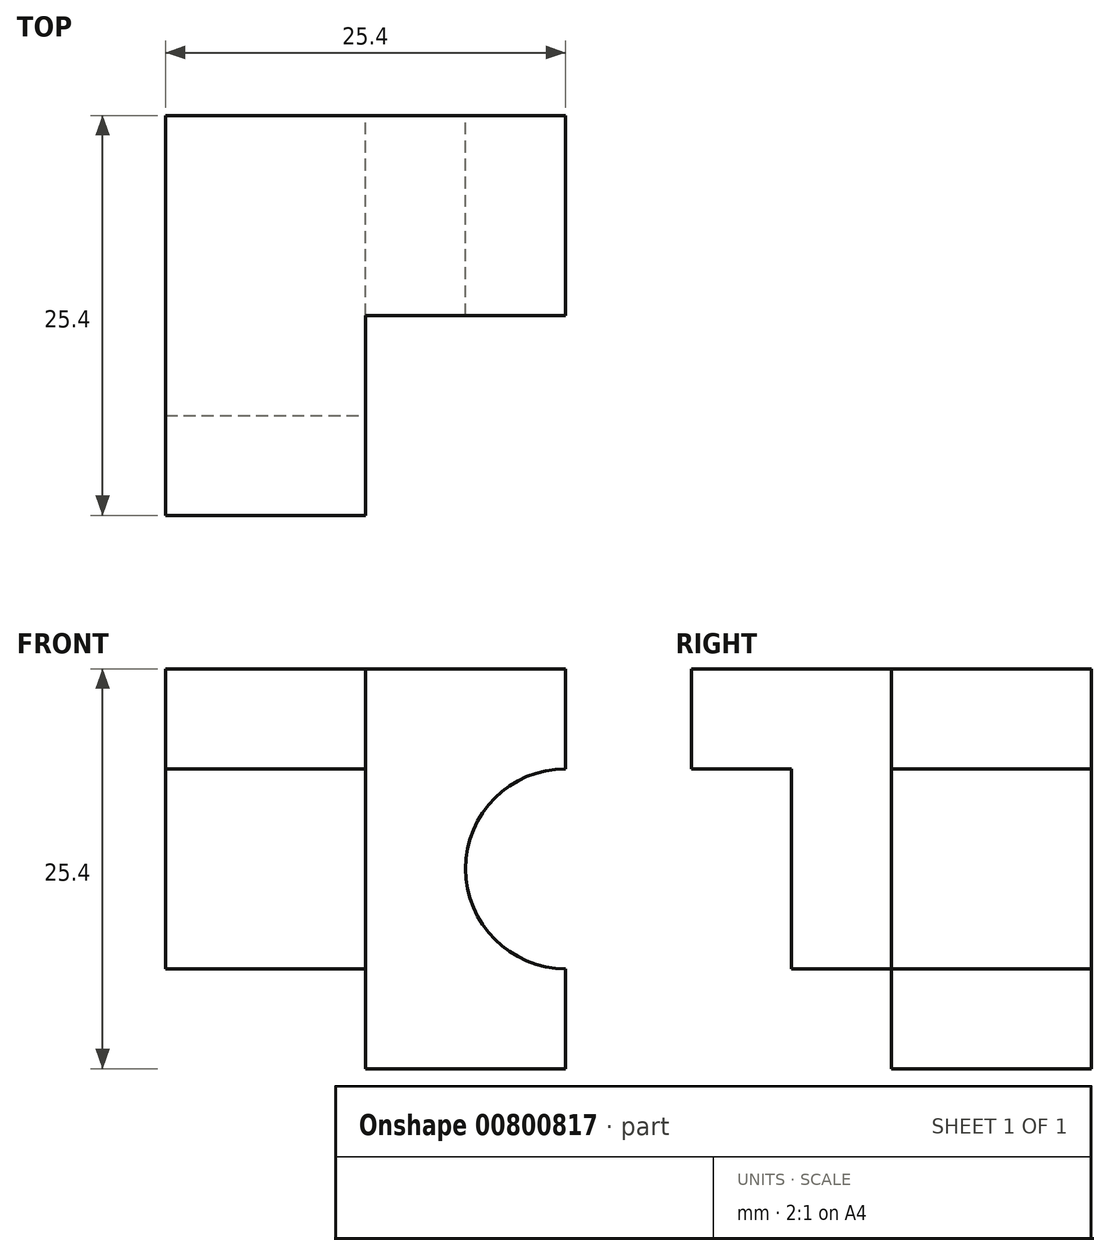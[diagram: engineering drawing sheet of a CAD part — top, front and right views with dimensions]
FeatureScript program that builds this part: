
annotation { "Feature Type Name" : "Feature", "Feature Type Description" : "" }
export const myFeature = defineFeature(function(context is Context, id is Id, definition is map)
    precondition{}
    {
        {
            var Q0;
            Q0=qCreatedBy(makeId("Front.planeOp"),FACE);
            var sketch = newSketch(context, id + "F0", { "sketchPlane" : qUnion([Q0])});
            skLineSegment(sketch, "E0", {"start": v(0, 0) * mm, "end": v(0, 25.4) * mm});
            skLineSegment(sketch, "E1", {"start": v(0, 25.4) * mm, "end": v(12.7, 25.4) * mm});
            skLineSegment(sketch, "E2", {"start": v(12.7, 25.4) * mm, "end": v(25.4, 25.4) * mm});
            skLineSegment(sketch, "E3", {"start": v(25.4, 25.4) * mm, "end": v(25.4, 0) * mm});
            skLineSegment(sketch, "E4", {"start": v(25.4, 0) * mm, "end": v(0, 0) * mm});
            skLineSegment(sketch, "E5", {"start": v(12.7, 25.4) * mm, "end": v(12.7, 0) * mm});
            skLineSegment(sketch, "E6", {"start": v(12.7, 0) * mm, "end": v(12.7, 6.35) * mm});
            skLineSegment(sketch, "E7", {"start": v(12.7, 6.35) * mm, "end": v(0, 6.35) * mm});
            skLineSegment(sketch, "E8", {"start": v(0, 6.35) * mm, "end": v(0, 19.05) * mm});
            skLineSegment(sketch, "E9", {"start": v(0, 19.05) * mm, "end": v(12.7, 19.05) * mm});
            skArc(sketch, "E10", {"start": v(25.4, 25.4) * mm, "mid": v(38.1, 12.7) * mm, "end": v(25.4, 0) * mm});
            skCircle(sketch, "E11", {"center": v(25.4, 12.7) * mm, "radius": 6.35 * mm});
            skSolve(sketch);
        }
        {
            var Q0;
            {var subQ7=sQuery(id+"F0.wireOp",EDGE,"E2");Q0=makeQuery(id+"F0.imprint","IMPRINT",FACE,{"disambiguationData":[TD([[makeQuery(id+"F0.imprint","IMPRINT",EDGE,{"derivedFrom":subQ7}),-1.0]])]});}
            var Q1;
            {var subQ0=sQuery(id+"F0.wireOp",EDGE,"E10");Q1=makeQuery(id+"F0.imprint","IMPRINT",FACE,{"disambiguationData":[TD([[makeQuery(id+"F0.imprint","IMPRINT",EDGE,{"derivedFrom":subQ0}),-1.0]])]});}
            extrude(context, id + "F1", {"entities" : qUnion([Q0, Q1]), "depth" : 12.7 * mm, "offsetDistance" : 25.4 * mm});
        }
        {
            var Q0;
            {var subQ0=sQuery(id+"F0.wireOp",EDGE,"E1");Q0=makeQuery(id+"F0.imprint","IMPRINT",FACE,{"disambiguationData":[TD([[makeQuery(id+"F0.imprint","IMPRINT",EDGE,{"derivedFrom":subQ0}),-1.0]])]});}
            var Q1;
            {var subQ4=sQuery(id+"F0.wireOp",EDGE,"E6");Q1=makeQuery(id+"F0.imprint","IMPRINT",FACE,{"disambiguationData":[TD([[makeQuery(id+"F0.imprint","IMPRINT",EDGE,{"derivedFrom":subQ4}),1.0]])]});}
            extrude(context, id + "F2", {"entities" : qUnion([Q0, Q1]), "operationType" : NewBodyOperationType.ADD, "depth" : 25.4 * mm, "offsetDistance" : 25.4 * mm});
        }
        {
            var Q0;
            {var subQ0=sQuery(id+"F0.wireOp",EDGE,"E7");Q0=makeQuery(id+"F0.imprint","IMPRINT",FACE,{"disambiguationData":[TD([[makeQuery(id+"F0.imprint","IMPRINT",EDGE,{"derivedFrom":subQ0}),-1.0]])]});}
            extrude(context, id + "F3", {"entities" : qUnion([Q0]), "operationType" : NewBodyOperationType.ADD, "depth" : 19.05 * mm, "offsetDistance" : 25.4 * mm});
        }
    });
